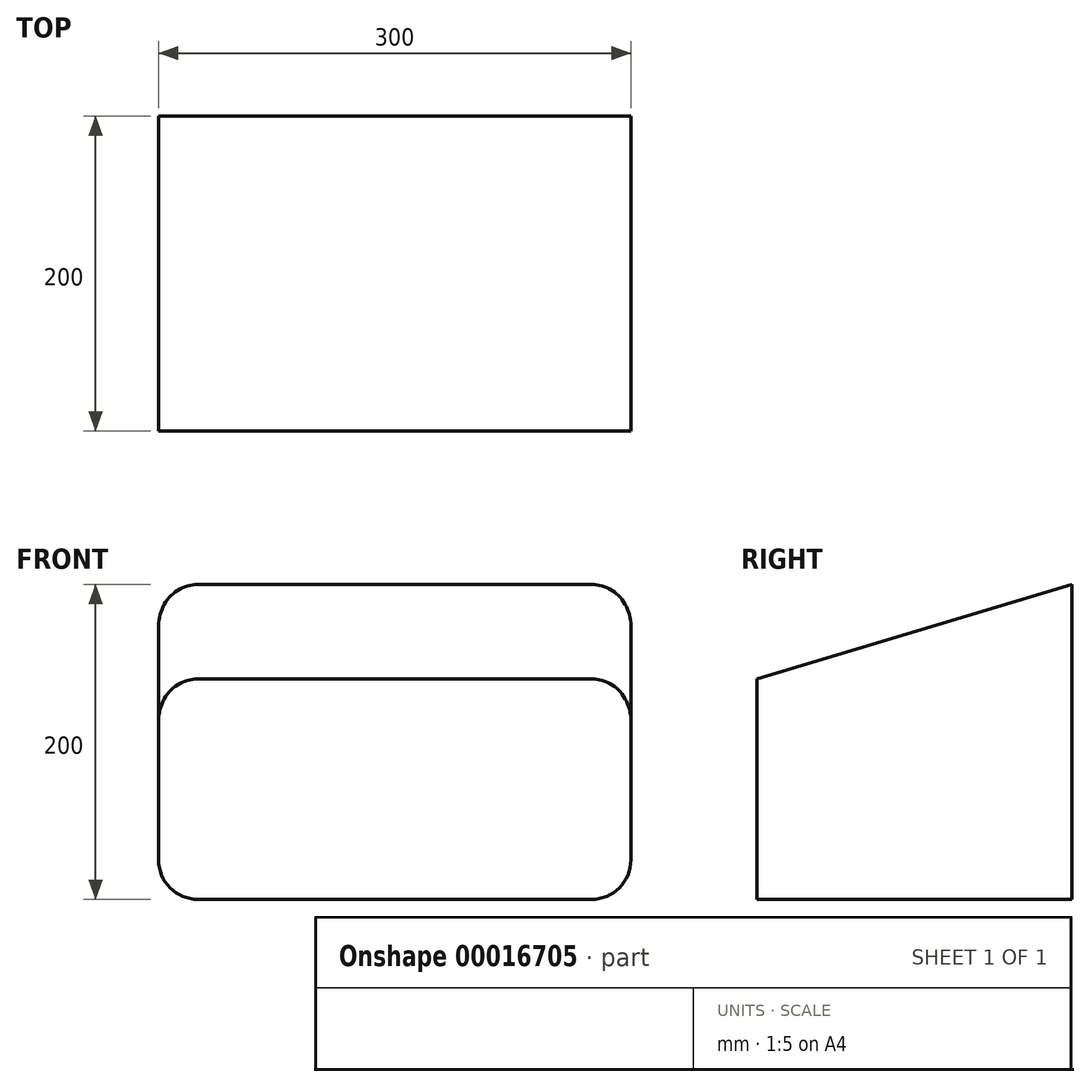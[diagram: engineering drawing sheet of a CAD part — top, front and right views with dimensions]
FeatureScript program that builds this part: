
annotation { "Feature Type Name" : "Feature", "Feature Type Description" : "" }
export const myFeature = defineFeature(function(context is Context, id is Id, definition is map)
    precondition{}
    {
        {
            var Q0;
            Q0=qCreatedBy(makeId("Right.planeOp"),FACE);
            var sketch = newSketch(context, id + "F0", { "sketchPlane" : qUnion([Q0])});
            skLineSegment(sketch, "E0", {"start": v(0, 0) * mm, "end": v(0, 100) * mm});
            skLineSegment(sketch, "E1", {"start": v(0, 100) * mm, "end": v(-200, 40) * mm});
            skLineSegment(sketch, "E2", {"start": v(-200, 40) * mm, "end": v(-200, -100) * mm});
            skLineSegment(sketch, "E3", {"start": v(-200, -100) * mm, "end": v(0, -100) * mm});
            skLineSegment(sketch, "E4", {"start": v(0, -100) * mm, "end": v(0, 0) * mm});
            skSolve(sketch);
        }
        {
            var Q0;
            Q0=makeQuery(id+"F0.imprint","IMPRINT",FACE,{"disambiguationData":[TD([[makeQuery(id+"F0.imprint","IMPRINT",EDGE,{"derivedFrom":sQuery(id+"F0.wireOp",EDGE,"E0")}),1.0]])]});
            extrude(context, id + "F1", {"entities" : qUnion([Q0]), "depth" : 300 * mm, "symmetric" : true});
        }
        {
            var Q0;
            Q0=makeQuery(id+"F1.opExtrude","CAP_EDGE",EDGE,{"disambiguationData":[OSD([sQuery(id+"F0.wireOp",EDGE,"E1")])],"isStart":false});
            var Q1;
            Q1=makeQuery(id+"F1.opExtrude","CAP_EDGE",EDGE,{"disambiguationData":[OSD([sQuery(id+"F0.wireOp",EDGE,"E1")])],"isStart":true});
            var Q2;
            Q2=makeQuery(id+"F1.opExtrude","CAP_EDGE",EDGE,{"disambiguationData":[OSD([sQuery(id+"F0.wireOp",EDGE,"E3")])],"isStart":false});
            var Q3;
            Q3=makeQuery(id+"F1.opExtrude","CAP_EDGE",EDGE,{"disambiguationData":[OSD([sQuery(id+"F0.wireOp",EDGE,"E3")])],"isStart":true});
            fillet(context, id + "F2", {"entities" : qUnion([Q0, Q1, Q2, Q3]), "radius" : 25 * mm, "tangentPropagation" : true, "allowEdgeOverflow" : false});
        }
    });
